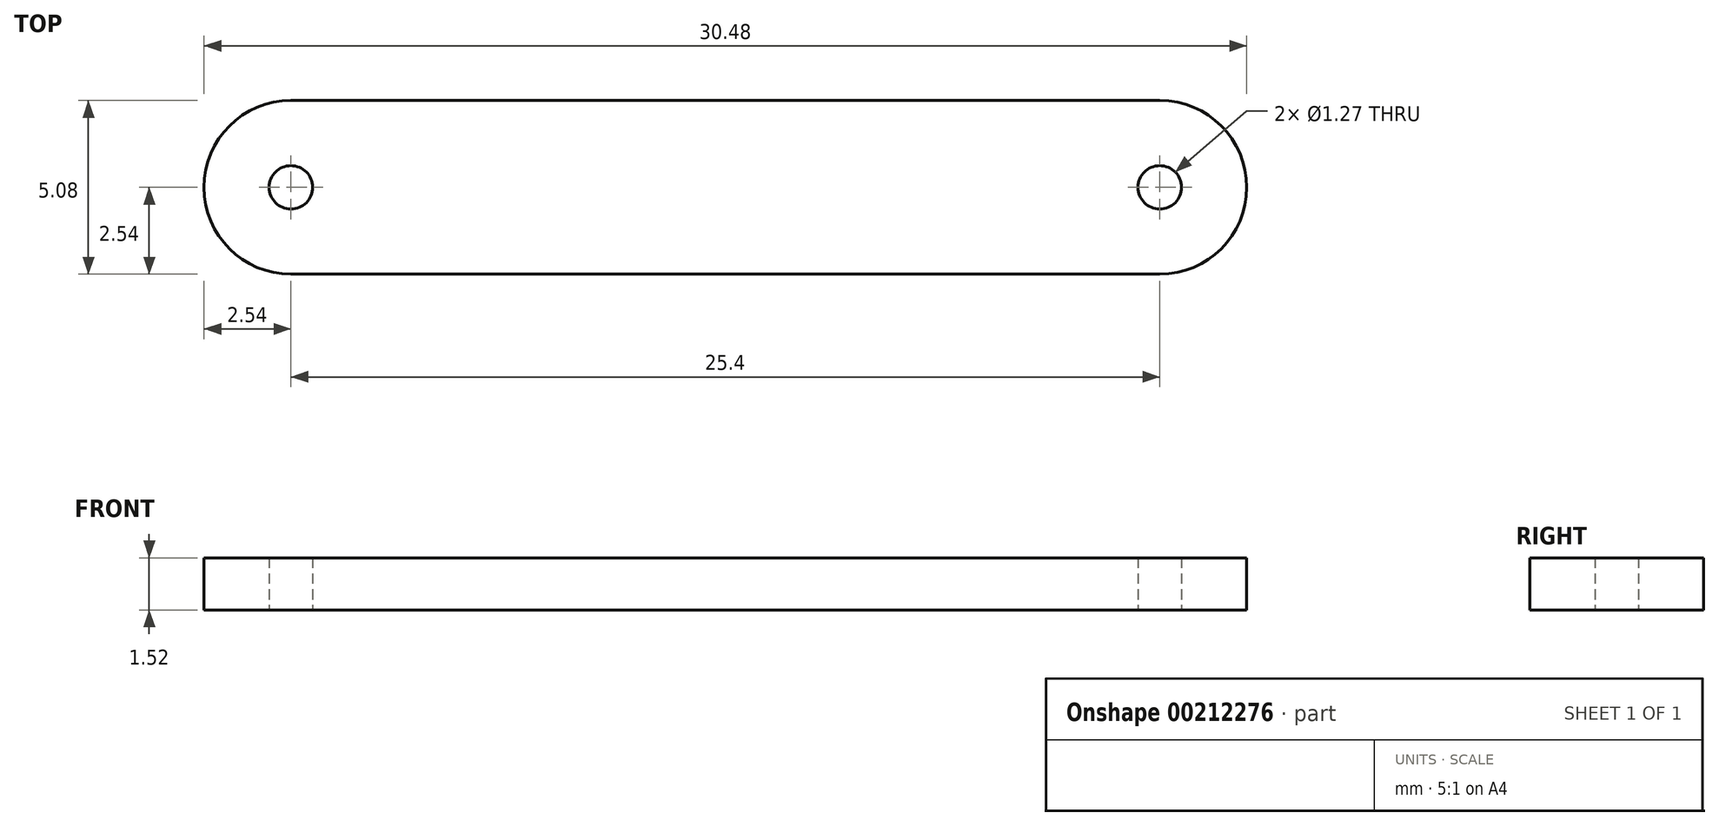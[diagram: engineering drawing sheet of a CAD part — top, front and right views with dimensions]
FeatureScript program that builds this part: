
annotation { "Feature Type Name" : "Feature", "Feature Type Description" : "" }
export const myFeature = defineFeature(function(context is Context, id is Id, definition is map)
    precondition{}
    {
        {
            var Q0;
            Q0=qCreatedBy(makeId("Top.planeOp"),FACE);
            var sketch = newSketch(context, id + "F0", { "sketchPlane" : qUnion([Q0])});
            skLineSegment(sketch, "E0.bottom", {"start": v(0, 0) * mm, "end": v(30.48, 0) * mm});
            skLineSegment(sketch, "E0.top", {"start": v(0, 5.08) * mm, "end": v(30.48, 5.08) * mm});
            skLineSegment(sketch, "E0.left", {"start": v(0, 0) * mm, "end": v(0, 5.08) * mm});
            skLineSegment(sketch, "E0.right", {"start": v(30.48, 0) * mm, "end": v(30.48, 5.08) * mm});
            skCircle(sketch, "E1", {"center": v(2.54, 2.54) * mm, "radius": 0.64 * mm});
            skCircle(sketch, "E2", {"center": v(27.94, 2.54) * mm, "radius": 0.64 * mm});
            skSolve(sketch);
        }
        {
            var Q0;
            Q0=makeQuery(id+"F0.imprint","IMPRINT",FACE,{"disambiguationData":[TD([[makeQuery(id+"F0.imprint","IMPRINT",EDGE,{"derivedFrom":sQuery(id+"F0.wireOp",EDGE,"E0.bottom")}),1.0]])]});
            extrude(context, id + "F1", {"entities" : qUnion([Q0]), "depth" : 1.52 * mm});
        }
        {
            var Q0;
            Q0=makeQuery(id+"F1.opExtrude","SWEPT_EDGE",EDGE,{"disambiguationData":[OSD([sQuery(id+"F0.wireOp",EDGE,"E0.bottom"),sQuery(id+"F0.wireOp",EDGE,"E0.left")])]});
            var Q1;
            Q1=makeQuery(id+"F1.opExtrude","SWEPT_EDGE",EDGE,{"disambiguationData":[OSD([sQuery(id+"F0.wireOp",EDGE,"E0.top"),sQuery(id+"F0.wireOp",EDGE,"E0.left")])]});
            var Q2;
            Q2=makeQuery(id+"F1.opExtrude","SWEPT_EDGE",EDGE,{"disambiguationData":[OSD([sQuery(id+"F0.wireOp",EDGE,"E0.bottom"),sQuery(id+"F0.wireOp",EDGE,"E0.right")])]});
            var Q3;
            Q3=makeQuery(id+"F1.opExtrude","SWEPT_EDGE",EDGE,{"disambiguationData":[OSD([sQuery(id+"F0.wireOp",EDGE,"E0.top"),sQuery(id+"F0.wireOp",EDGE,"E0.right")])]});
            fillet(context, id + "F2", {"entities" : qUnion([Q0, Q1, Q2, Q3]), "radius" : 2.54 * mm, "tangentPropagation" : true, "allowEdgeOverflow" : false});
        }
    });
